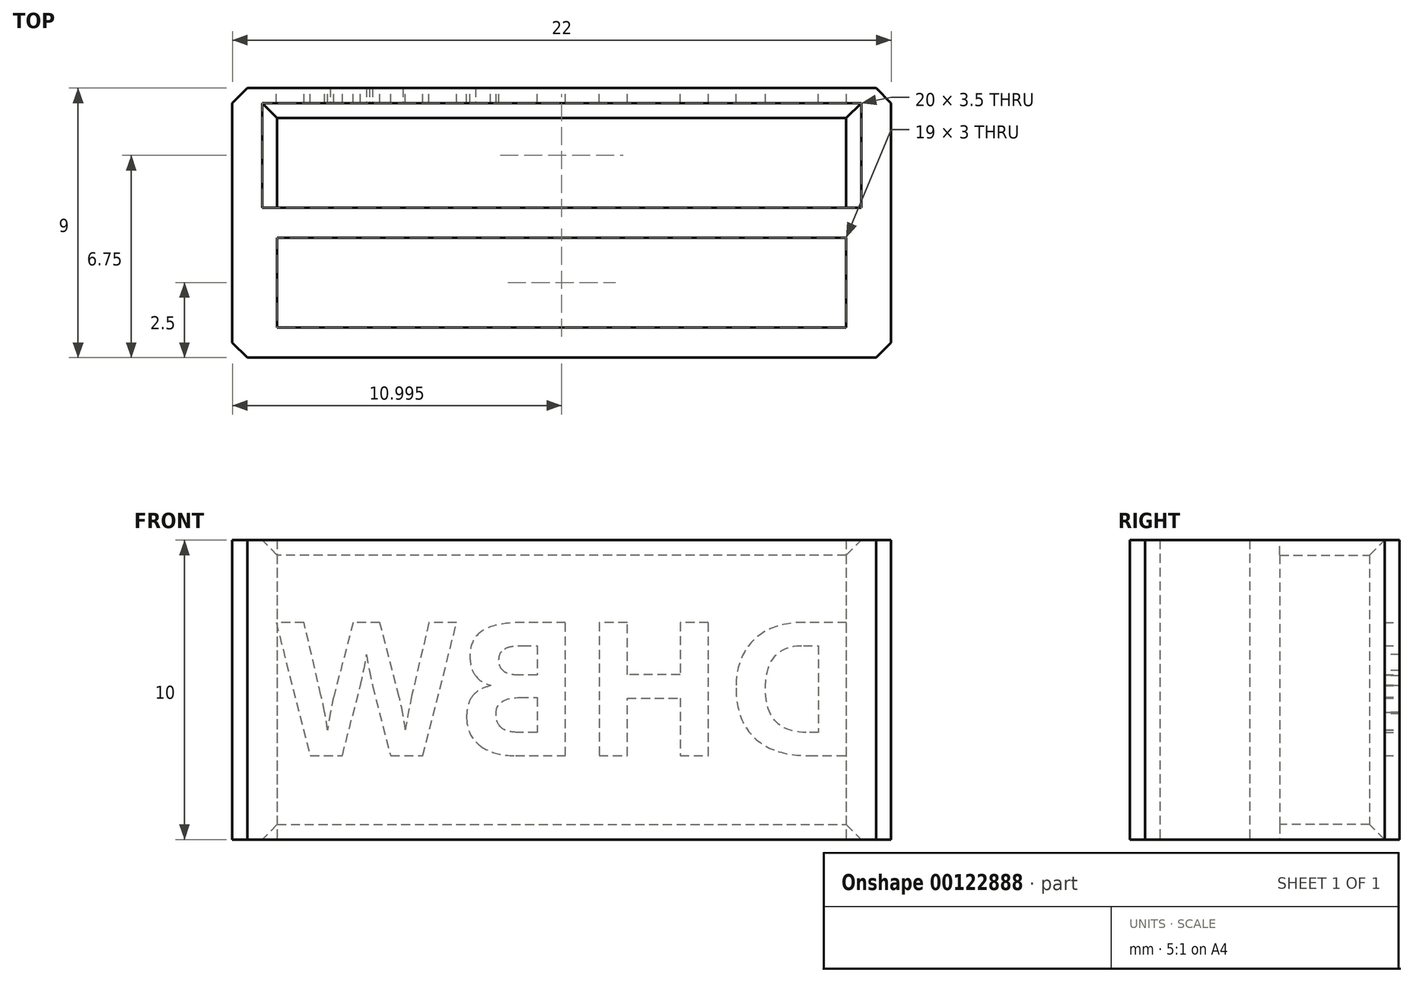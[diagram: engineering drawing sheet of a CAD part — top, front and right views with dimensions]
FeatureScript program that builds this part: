
annotation { "Feature Type Name" : "Feature", "Feature Type Description" : "" }
export const myFeature = defineFeature(function(context is Context, id is Id, definition is map)
    precondition{}
    {
        {
            var Q0;
            Q0=qCreatedBy(makeId("Top.planeOp"),FACE);
            var sketch = newSketch(context, id + "F0", { "sketchPlane" : qUnion([Q0])});
            skLineSegment(sketch, "E0.bottom", {"start": v(-11.57, 1) * mm, "end": v(7.43, 1) * mm});
            skLineSegment(sketch, "E0.top", {"start": v(-11.57, 0) * mm, "end": v(7.93, 0) * mm});
            skLineSegment(sketch, "E1.top", {"start": v(-11.57, 4) * mm, "end": v(7.43, 4) * mm});
            skLineSegment(sketch, "E1.left", {"start": v(-11.57, 1) * mm, "end": v(-11.57, 4) * mm});
            skLineSegment(sketch, "E1.right", {"start": v(7.43, 1) * mm, "end": v(7.43, 4) * mm});
            skLineSegment(sketch, "E2.top", {"start": v(7.43, 0) * mm, "end": v(8.93, 0) * mm});
            skLineSegment(sketch, "E2.left", {"start": v(7.43, 4) * mm, "end": v(7.43, 1) * mm});
            skLineSegment(sketch, "E2.right", {"start": v(8.93, 4) * mm, "end": v(8.93, 0) * mm});
            skLineSegment(sketch, "E3.top", {"start": v(-11.57, 0) * mm, "end": v(-13.07, 0) * mm});
            skLineSegment(sketch, "E3.left", {"start": v(-11.57, 4) * mm, "end": v(-11.57, 1) * mm});
            skLineSegment(sketch, "E3.right", {"start": v(-13.07, 4) * mm, "end": v(-13.07, 0) * mm});
            skLineSegment(sketch, "E4.bottom", {"start": v(7.43, 4) * mm, "end": v(-11.57, 4) * mm});
            skLineSegment(sketch, "E4.top", {"start": v(8.93, 5) * mm, "end": v(-11.57, 5) * mm});
            skLineSegment(sketch, "E4.left", {"start": v(8.93, 4) * mm, "end": v(8.93, 5) * mm});
            skLineSegment(sketch, "E4.right", {"start": v(-13.07, 4) * mm, "end": v(-13.07, 5) * mm});
            skLineSegment(sketch, "E5.bottom", {"start": v(-11.57, 5) * mm, "end": v(7.43, 5) * mm});
            skLineSegment(sketch, "E5.top", {"start": v(-13.07, 9) * mm, "end": v(8.93, 9) * mm});
            skLineSegment(sketch, "E5.left", {"start": v(-13.07, 5) * mm, "end": v(-13.07, 9) * mm});
            skLineSegment(sketch, "E5.right", {"start": v(8.93, 5) * mm, "end": v(8.93, 9) * mm});
            skLineSegment(sketch, "E6.top", {"start": v(-11.57, 8) * mm, "end": v(7.43, 8) * mm});
            skLineSegment(sketch, "E6.left", {"start": v(-11.57, 5) * mm, "end": v(-11.57, 8) * mm});
            skLineSegment(sketch, "E6.right", {"start": v(7.43, 5) * mm, "end": v(7.43, 8) * mm});
            skSolve(sketch);
        }
        {
            var Q0;
            {var subQ0=sQuery(id+"F0.wireOp",EDGE,"E0.top");Q0=makeQuery(id+"F0.imprint","IMPRINT",FACE,{"disambiguationData":[TD([[makeQuery(id+"F0.imprint","IMPRINT",EDGE,{"derivedFrom":subQ0}),1.0]])]});}
            extrude(context, id + "F1", {"entities" : qUnion([Q0]), "depth" : 10 * mm});
        }
        {
            var Q0;
            Q0=makeQuery(id+"F1.opExtrude","SWEPT_EDGE",EDGE,{"disambiguationData":[OSD([sQuery(id+"F0.wireOp",EDGE,"E5.top"),sQuery(id+"F0.wireOp",EDGE,"E5.left")])]});
            var Q1;
            Q1=makeQuery(id+"F1.opExtrude","SWEPT_EDGE",EDGE,{"disambiguationData":[OSD([sQuery(id+"F0.wireOp",EDGE,"E3.top"),sQuery(id+"F0.wireOp",EDGE,"E3.right")])]});
            var Q2;
            Q2=makeQuery(id+"F1.opExtrude","SWEPT_EDGE",EDGE,{"disambiguationData":[OSD([sQuery(id+"F0.wireOp",EDGE,"E5.top"),sQuery(id+"F0.wireOp",EDGE,"E5.right")])]});
            var Q3;
            Q3=makeQuery(id+"F1.opExtrude","SWEPT_EDGE",EDGE,{"disambiguationData":[OSD([sQuery(id+"F0.wireOp",EDGE,"E2.top"),sQuery(id+"F0.wireOp",EDGE,"E2.right")])]});
            chamfer(context, id + "F2", {"entities" : qUnion([Q0, Q1, Q2, Q3]), "width" : 0.5 * mm, "tangentPropagation" : true});
        }
        {
            var Q0;
            Q0=makeQuery(id+"F1.opExtrude","CAP_EDGE",EDGE,{"disambiguationData":[OSD([sQuery(id+"F0.wireOp",EDGE,"E6.top")])],"isStart":false});
            var Q1;
            Q1=makeQuery(id+"F1.opExtrude","CAP_EDGE",EDGE,{"disambiguationData":[OSD([sQuery(id+"F0.wireOp",EDGE,"E6.left")])],"isStart":false});
            var Q2;
            Q2=makeQuery(id+"F1.opExtrude","CAP_EDGE",EDGE,{"disambiguationData":[OSD([sQuery(id+"F0.wireOp",EDGE,"E5.bottom")])],"isStart":false});
            var Q3;
            Q3=makeQuery(id+"F1.opExtrude","CAP_EDGE",EDGE,{"disambiguationData":[OSD([sQuery(id+"F0.wireOp",EDGE,"E6.right")])],"isStart":false});
            var Q4;
            Q4=makeQuery(id+"F1.opExtrude","CAP_EDGE",EDGE,{"disambiguationData":[OSD([sQuery(id+"F0.wireOp",EDGE,"E2.left")])],"isStart":false});
            var Q5;
            Q5=makeQuery(id+"F1.opExtrude","CAP_EDGE",EDGE,{"disambiguationData":[OSD([sQuery(id+"F0.wireOp",EDGE,"E4.bottom")])],"isStart":false});
            var Q6;
            Q6=makeQuery(id+"F1.opExtrude","CAP_EDGE",EDGE,{"disambiguationData":[OSD([sQuery(id+"F0.wireOp",EDGE,"E0.bottom")])],"isStart":false});
            var Q7;
            Q7=makeQuery(id+"F1.opExtrude","CAP_EDGE",EDGE,{"disambiguationData":[OSD([sQuery(id+"F0.wireOp",EDGE,"E3.left")])],"isStart":false});
            chamfer(context, id + "F3", {"entities" : qUnion([Q0, Q1, Q2, Q3, Q4, Q5, Q6, Q7]), "width" : 0.5 * mm, "tangentPropagation" : true});
        }
        {
            var Q0;
            Q0=makeQuery(id+"F1.opExtrude","CAP_EDGE",EDGE,{"disambiguationData":[OSD([sQuery(id+"F0.wireOp",EDGE,"E6.top")])],"isStart":true});
            var Q1;
            Q1=makeQuery(id+"F1.opExtrude","CAP_EDGE",EDGE,{"disambiguationData":[OSD([sQuery(id+"F0.wireOp",EDGE,"E6.right")])],"isStart":true});
            var Q2;
            Q2=makeQuery(id+"F1.opExtrude","CAP_EDGE",EDGE,{"disambiguationData":[OSD([sQuery(id+"F0.wireOp",EDGE,"E5.bottom")])],"isStart":true});
            var Q3;
            Q3=makeQuery(id+"F1.opExtrude","CAP_EDGE",EDGE,{"disambiguationData":[OSD([sQuery(id+"F0.wireOp",EDGE,"E6.left")])],"isStart":true});
            var Q4;
            Q4=makeQuery(id+"F1.opExtrude","CAP_EDGE",EDGE,{"disambiguationData":[OSD([sQuery(id+"F0.wireOp",EDGE,"E3.left")])],"isStart":true});
            var Q5;
            Q5=makeQuery(id+"F1.opExtrude","CAP_EDGE",EDGE,{"disambiguationData":[OSD([sQuery(id+"F0.wireOp",EDGE,"E4.bottom")])],"isStart":true});
            var Q6;
            Q6=makeQuery(id+"F1.opExtrude","CAP_EDGE",EDGE,{"disambiguationData":[OSD([sQuery(id+"F0.wireOp",EDGE,"E2.left")])],"isStart":true});
            var Q7;
            Q7=makeQuery(id+"F1.opExtrude","CAP_EDGE",EDGE,{"disambiguationData":[OSD([sQuery(id+"F0.wireOp",EDGE,"E0.bottom")])],"isStart":true});
            chamfer(context, id + "F4", {"entities" : qUnion([Q0, Q1, Q2, Q3, Q4, Q5, Q6, Q7]), "width" : 0.5 * mm, "tangentPropagation" : true});
        }
        {
            var Q0;
            Q0=makeQuery(id+"F1.opExtrude","SWEPT_FACE",FACE,{"disambiguationData":[OSD([sQuery(id+"F0.wireOp",EDGE,"E5.top")])]});
            var sketch = newSketch(context, id + "F5", { "sketchPlane" : qUnion([Q0])});
            skText(sketch, "E7", { "text": "DHBW", "fontName": "OpenSans-Bold.ttf"});
            const initialGuessF5  = {"E7": [-0.008, 0.0028, 1, 0, 0.00449]};
            skSetInitialGuess(sketch, initialGuessF5);
            skSolve(sketch);
        }
        {
            var Q0;
            Q0 = qSketchRegion(id + "F5", true);
            extrude(context, id + "F6", {"entities" : qUnion([Q0]), "operationType" : NewBodyOperationType.REMOVE, "oppositeDirection" : true, "depth" : 0.5 * mm});
        }
    });
